# Revit family: P710069-009
name_source: partatom
category: Lighting Fixtures
revit_build: Autodesk Revit 2014 (Build: 20130308_1515(x64)
units: mm (PartAtom-declared; Revit-internal decimal feet)

## types (1)
- P710069-009
    Apparent Load = 60 VA
    Assembly Code = D5020200
    Color Filter = 16777215
    Connector Description = Lighting Connector
    Default Elevation = 48"
    Description = The Lookout wall sconce has a modern classic styling that combines Brushed Nickel, clear seeded glass and handsome leather accents for an enduring sensibility that adds an uncomplicated elegance to any interior. Entirely at home in so many locations and lifestyles, the Lookout sconce is ideal to use when multiples are a must. This fixture is part of the Jeffrey Alan Marks Point Dume™ lighting collection which celebrates a curated mix of yesterday and today, distilling both industrial and artisanal influences.
    Dimming Lamp Color Temperature Shift = <None>
    Features = Wall sconce with unique topstitched brown leather back plate and handsome leather-trimmed handle.
Line shines through a cylinder shade of seeded glass, banded top and bottom with Brushed Nickel.
Shade is suspended from parallel cut metal arms fastened by a riveted, brown leather strap handle.
Use restoration-style filament bulbs for added sophistication.
Use anywhere there is a need for more ambient or task light, or where floor space is at a premium.
Try in multiples along a hallway, in pairs bedside, flanking a fireplace or bath vanity, or in more traditional spaces such as a dining room to coordinate with the overhead lighting.
With its substantial form and bespoke leather detailing adding a touch of personality, Lookout is perfect for warmer Modern interiors.
A classic wall sconce design combined with unique bespoke leather detailing blends old with new, creating a New Traditional look that is both timeless and timely.
Finished in a subtly reflective Brushed Nickel for an elegant matte texture effect, offsetting clear seeded glass shade and brown leather detailing.
This oversized wall sconce is 6 in. wide and 12.875 in. high, with a depth of 7.375 in.
Use one, 60w max. candelabra medium base bulb incandescent or LED equivalent wattage bulbs (bulbs not included).
For an alternate look, try Edison bulbs or other vintage-style filament bulbs (bulbs not included).
    Fixture distribution = Direct
    Glass = Hubbell - Glass
    Height = 12 7/8"
    Housing Material = Paint - Hubbell - Textured Camera Black
    Lamp = A-19
    Load Classification = Lighting
    Manufacturer = Progress Lighting
    Model = P710069-009
    Photometric Web File = generic
    Power Factor = 1
    Product Documentation Link = https://hubbellcdn.com
    Product Link = https://www.hubbell.com
    Silver = Paint - Hubbell - Light Silver
    Tilt Angle = 60.00°
    URL = https://www.hubbell.com
    Voltage = 120 V
    Warranty = 5 years Warranty
    Wattage Comments = 60W
    Watts = 60 W
    Width = 6"

## geometry (parser evidence)
native form markers: Sweep x4
no freeform markers — native parametric forms only
